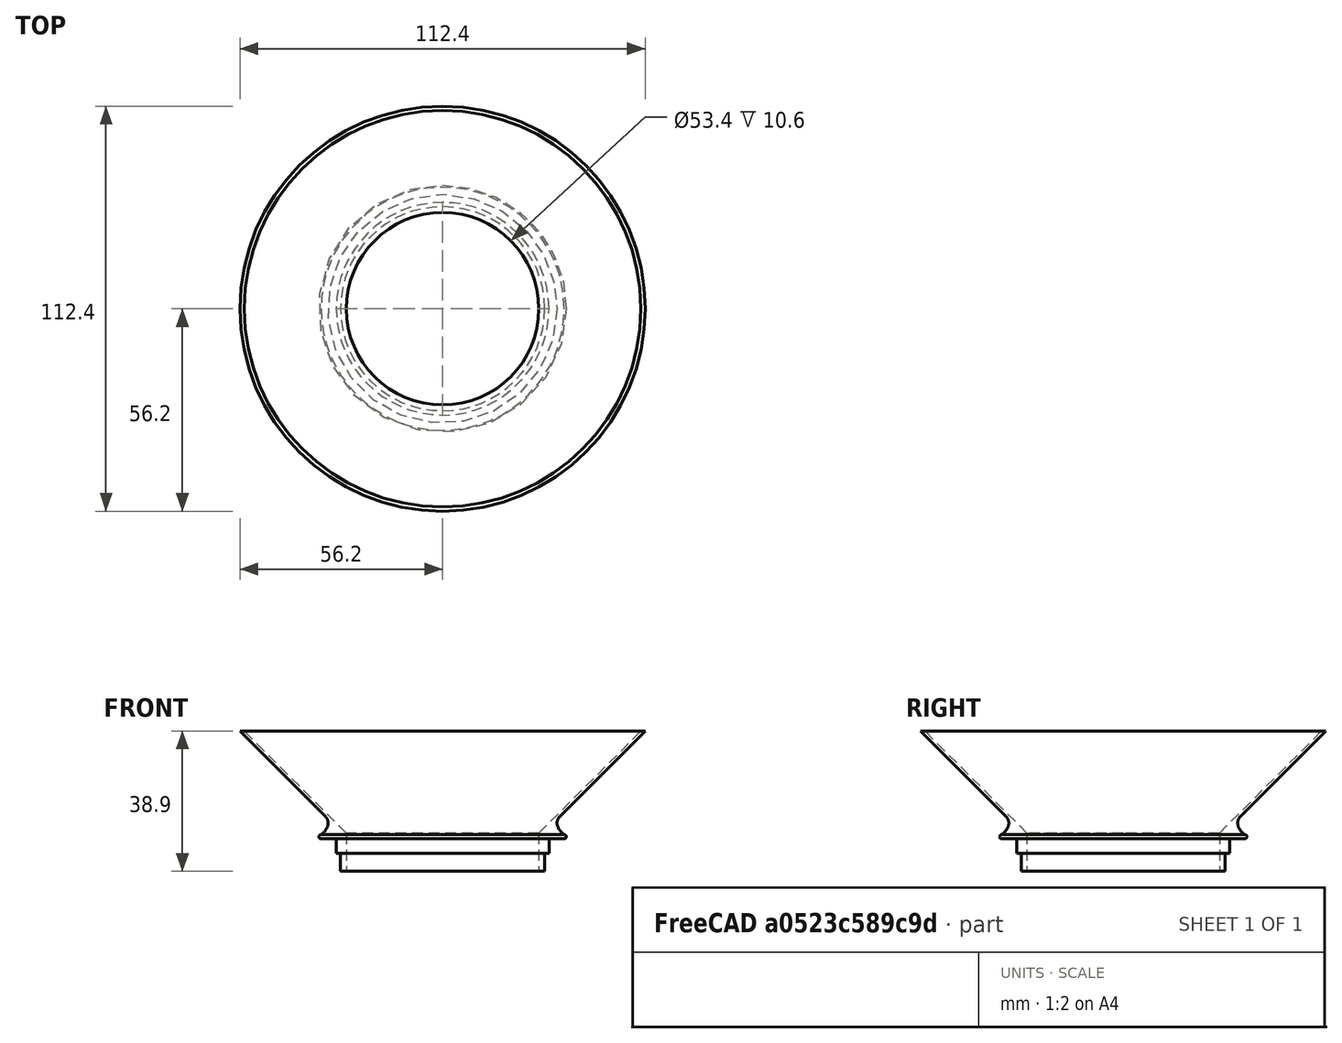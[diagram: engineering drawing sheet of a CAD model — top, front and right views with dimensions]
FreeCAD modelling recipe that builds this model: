
FCSTD DOCUMENT  (FreeCAD 0.19R19443 (Git))
Label: envudo
License: All rights reserved
LicenseURL: http://en.wikipedia.org/wiki/All_rights_reserved
objects: Sketcher::SketchObject×1, PartDesign::Revolution×1, PartDesign::Body×1
note: 4 computed .brp shape members not serialized (recipe doc carries the construction recipe); baked Part::Feature solids carry a one-line shape summary decoded from their .brp

FEATURE [Sketcher::SketchObject] Sketch
  MapMode = 5
  Placement = pos=(0,0,0) rot=(1,0,0;1.5708rad)
  Support = -> [XZ_Plane]
  expr: Constraints[14] = (60 - 1) / 2
  expr: Constraints[32] = 180 - 45
  sketch-geometry (12):
    g0: LineSegment StartX=28.3 StartY=0 StartZ=0 EndX=28.3 EndY=5 EndZ=0
    g1: LineSegment StartX=26.7 StartY=10.6 StartZ=0 EndX=26.7 EndY=0 EndZ=0
    g2: LineSegment StartX=26.7 StartY=0 StartZ=0 EndX=28.3 EndY=0 EndZ=0
    g3: LineSegment StartX=29.5 StartY=9 StartZ=0 EndX=29.5 EndY=5 EndZ=0
    g4: LineSegment StartX=29.5 StartY=5 StartZ=0 EndX=28.3 EndY=5 EndZ=0
    g5: LineSegment StartX=26.7 StartY=10.6 StartZ=0 EndX=55 EndY=38.9 EndZ=0
    g6: LineSegment StartX=55 StartY=38.9 StartZ=0 EndX=56.2 EndY=38.9 EndZ=0
    g7: LineSegment StartX=56.2 StartY=38.9 StartZ=0 EndX=32.4721 EndY=15.1721 EndZ=0
    g8: LineSegment StartX=29.5 StartY=9 StartZ=0 EndX=33.7 EndY=9 EndZ=0
    g9: ArcOfCircle CenterX=36.2 CenterY=14 CenterZ=0 NormalX=0 NormalY=0 NormalZ=1 AngleXU=0 Radius=4.54863 StartAngle=3.43661 EndAngle=4.13048
    g10: ArcOfCircle CenterX=34.2399 CenterY=13.4043 CenterZ=0 NormalX=0 NormalY=0 NormalZ=1 AngleXU=0 Radius=2.5 StartAngle=2.35619 EndAngle=3.43661
    g11: ArcOfCircle CenterX=33.7 CenterY=9.6 CenterZ=0 NormalX=0 NormalY=0 NormalZ=1 AngleXU=0 Radius=0.6 StartAngle=4.71239 EndAngle=7.85398
  constraints (37):
    c: PointOnObject(g0,g-1)
    c: Vertical(g0)
    c: Vertical(g1)
    c: Coincident(g1,g2)
    c: Coincident(g2,g0)
    c: Horizontal(g2)
    c: DistanceX(g2,g2) = 1.6
    c: DistanceY(g0,g0) = 5
    c: Coincident(g3,g4)
    c: Coincident(g4,g0)
    c: Vertical(g3)
    c: Horizontal(g4)
    c: DistanceX(g4,g4) = 1.2
    c: DistanceY(g3,g3) = 4
    c: DistanceX(g-1,g3) = 29.5
    c: DistanceY(g3,g1) = 1.6
    c: Coincident(g1,g5)
    c: Coincident(g5,g6)
    c: Coincident(g6,g7)
    c: Parallel(g5,g7)
    c: Horizontal(g6,g5)
    c: Coincident(g8,g3)
    c: Horizontal(g8)
    c: DistanceX(g1,g8) = 7
    c: Vertical(g9,g8)
    c: DistanceY(g8,g9) = 1.2
    c: Tangent(g9,g10) = -1.5708
    c: Tangent(g7,g10) = -1.5708
    c: DistanceX(g6,g6) = 1.2
    c: Coincident(g11,g9)
    c: Coincident(g11,g8)
    c: Vertical(g9,g11)
    c: Angle(g1,g5) = 2.35619
    c: DistanceY(g8,g9) = 5
    c: DistanceX(g9,g9) = 2.5
    c: Radius(g10) = 2.5
    c: DistanceX(g-1,g5) = 55
FEATURE [PartDesign::Revolution] Revolution
  Angle = 360
  Axis = (0,-2e-16,1)
  Base = (0,0,0)
  Placement = pos=(0,0,0) rot=(1,0,0;1.5708rad)
  Profile = -> Sketch
  ReferenceAxis = -> Sketch [V_Axis]
  Reversed = true
FEATURE [PartDesign::Body] Body
  Group = -> [Sketch,Revolution]
  Origin = -> Origin
  Tip = -> Revolution
